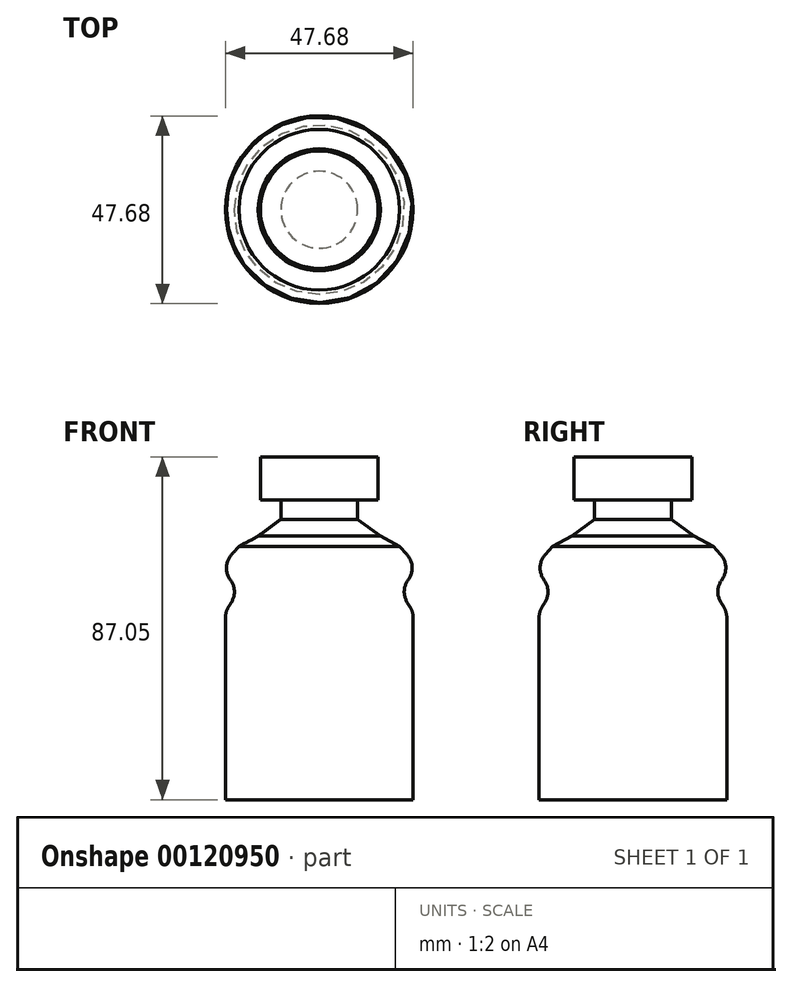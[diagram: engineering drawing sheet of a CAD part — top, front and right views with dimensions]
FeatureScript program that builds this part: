
annotation { "Feature Type Name" : "Feature", "Feature Type Description" : "" }
export const myFeature = defineFeature(function(context is Context, id is Id, definition is map)
    precondition{}
    {
        {
            var Q0;
            Q0=qCreatedBy(makeId("Front.planeOp"),FACE);
            var sketch = newSketch(context, id + "F0", { "sketchPlane" : qUnion([Q0])});
            skLineSegment(sketch, "E0", {"start": v(0, 59.9) * mm, "end": v(-14.94, 59.9) * mm});
            skLineSegment(sketch, "E1", {"start": v(-14.94, 59.9) * mm, "end": v(-14.94, 48.98) * mm});
            skLineSegment(sketch, "E2", {"start": v(-14.94, 48.98) * mm, "end": v(-9.77, 48.98) * mm});
            skLineSegment(sketch, "E3", {"start": v(-9.77, 48.98) * mm, "end": v(-9.77, 44.1) * mm});
            skLineSegment(sketch, "E4", {"start": v(-9.77, 44.1) * mm, "end": v(-15.51, 39.79) * mm});
            skLineSegment(sketch, "E5", {"start": v(-20.11, 26.57) * mm, "end": v(-23.84, 20.54) * mm});
            skLineSegment(sketch, "E6", {"start": v(-23.84, 20.54) * mm, "end": v(-23.84, -4.17) * mm});
            skLineSegment(sketch, "E7", {"start": v(-23.84, -4.17) * mm, "end": v(-23.84, -27.15) * mm});
            skLineSegment(sketch, "E8", {"start": v(-23.84, -27.15) * mm, "end": v(0, -27.15) * mm});
            skLineSegment(sketch, "E9", {"start": v(0, -27.15) * mm, "end": v(0, 59.9) * mm});
            skLineSegment(sketch, "E10", {"start": v(-15.51, 39.79) * mm, "end": v(-20.4, 37.2) * mm});
            skLineSegment(sketch, "E11", {"start": v(-20.4, 37.2) * mm, "end": v(-25.56, 31.53) * mm});
            skLineSegment(sketch, "E12", {"start": v(-25.56, 31.53) * mm, "end": v(-20.11, 26.57) * mm});
            skLineSegment(sketch, "E13", {"start": v(-20.11, 26.57) * mm, "end": v(-20.11, 26.57) * mm});
            skSolve(sketch);
        }
        {
            var Q0;
            Q0 = qSketchRegion(id + "F0", true);
            var Q1;
            Q1=sQuery(id+"F0.wireOp",EDGE,"E9");
            revolve(context, id + "F1", {"entities" : qUnion([Q0]), "axis" : qUnion([Q1]), "revolveType" : RevolveType.FULL});
        }
        {
            var Q0;
            Q0=makeQuery(id+"F1.opRevolve","SWEPT_FACE",FACE,{"disambiguationData":[OSD([sQuery(id+"F0.wireOp",EDGE,"E5")])]});
            fillet(context, id + "F2", {"entities" : qUnion([Q0]), "radius" : 5.08 * mm, "tangentPropagation" : true, "allowEdgeOverflow" : false});
        }
        {
            var Q0;
            Q0=makeQuery(id+"F1.opRevolve","SWEPT_EDGE",EDGE,{"disambiguationData":[OSD([sQuery(id+"F0.wireOp",EDGE,"E11"),sQuery(id+"F0.wireOp",EDGE,"E12")])]});
            fillet(context, id + "F3", {"entities" : qUnion([Q0]), "radius" : 5.08 * mm, "tangentPropagation" : true, "allowEdgeOverflow" : false});
        }
    });
